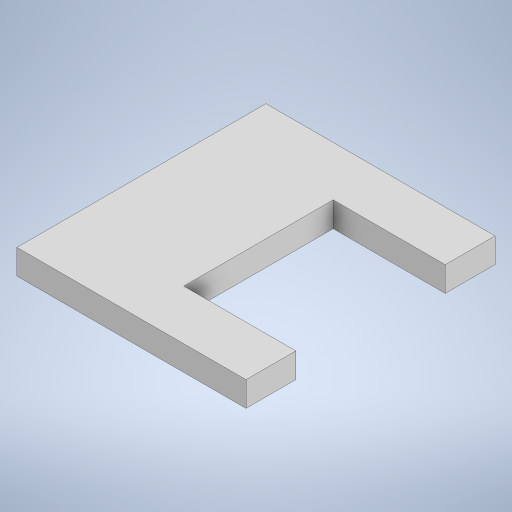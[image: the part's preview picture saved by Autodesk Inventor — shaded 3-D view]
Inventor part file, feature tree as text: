
AUTODESK INVENTOR PART (.ipt)
format: ipt  version: 2024 (Build 280153000, 153)  size: 226,304 bytes
history: native  units: mm
features: sketch x3, extrude x2
ambient origin geometry x8: Origin, YZ Plane, XZ Plane, XY Plane, X Axis, Y Axis, Z Axis, Center Point
bodies: Solid1 (feature_tree)
feature tree (5):
  sketch  "Sketch1"  dims[d0=100.0mm d1=92.0mm]
  extrude  "Extrusion1"  Depth=92.0mm
  extrude  "Extrusion2"  Depth=60.0mm
  sketch  "Sketch2"  dims[d2=10.0mm d3=0.0mm d4=60.0mm]
  sketch  "Sketch3"  dims[d5=20.0mm d6=20.0mm d7=45.0mm d8=100.0mm d9=0.0mm]
